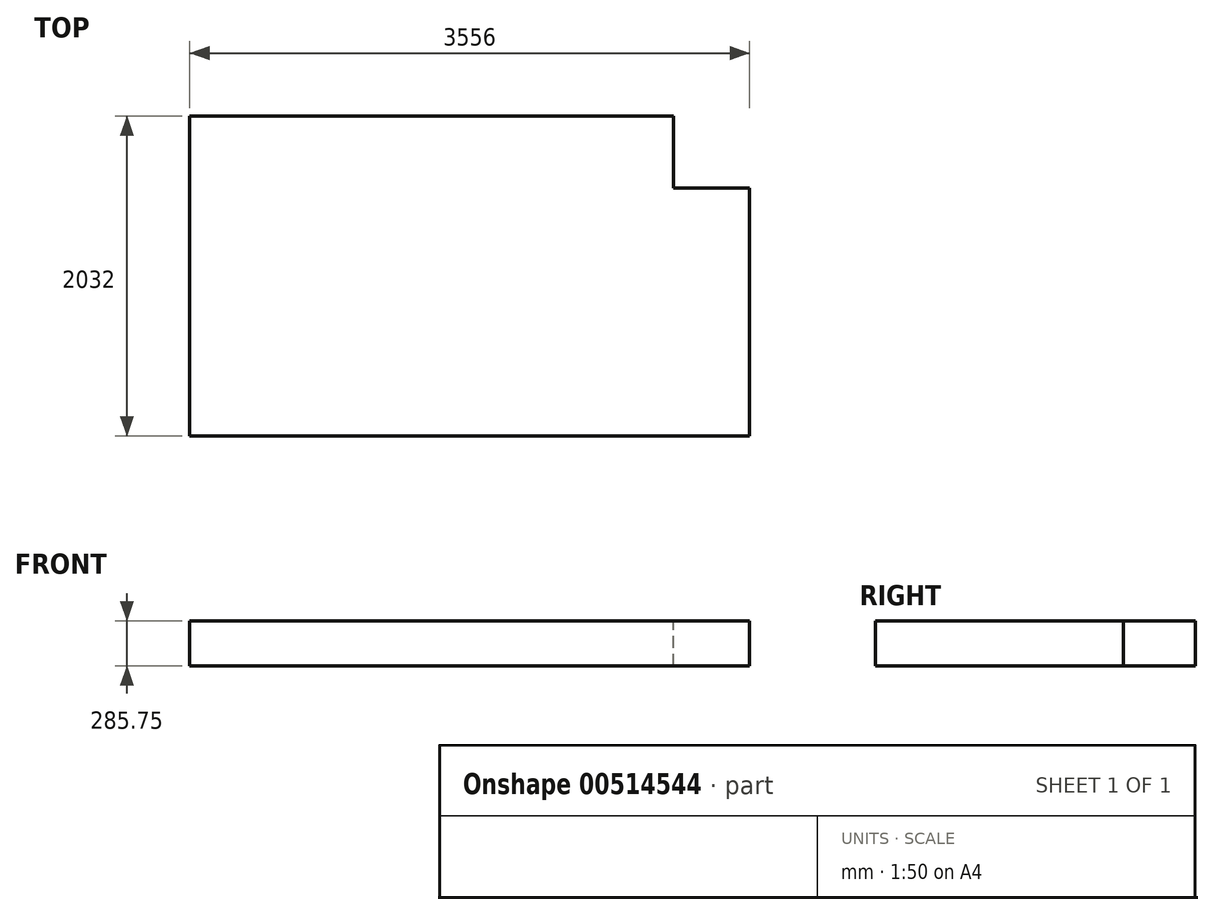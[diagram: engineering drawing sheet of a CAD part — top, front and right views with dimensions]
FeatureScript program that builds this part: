
annotation { "Feature Type Name" : "Feature", "Feature Type Description" : "" }
export const myFeature = defineFeature(function(context is Context, id is Id, definition is map)
    precondition{}
    {
        {
            var Q0;
            Q0=qCreatedBy(makeId("Top.planeOp"),FACE);
            var sketch = newSketch(context, id + "F0", { "sketchPlane" : qUnion([Q0])});
            skLineSegment(sketch, "E0.bottom", {"start": v(1700.43, 1002.82) * mm, "end": v(-1855.57, 1002.82) * mm});
            skLineSegment(sketch, "E0.top", {"start": v(1700.43, -1029.18) * mm, "end": v(-1855.57, -1029.18) * mm});
            skLineSegment(sketch, "E0.left", {"start": v(1700.43, 1002.82) * mm, "end": v(1700.43, -1029.18) * mm});
            skLineSegment(sketch, "E0.right", {"start": v(-1855.57, 1002.82) * mm, "end": v(-1855.57, -1029.18) * mm});
            skPoint(sketch, "E0.middle", {"position": v(-77.57, -13.18) * mm});
            skSolve(sketch);
        }
        {
            var Q0;
            Q0=makeQuery(id+"F0.imprint","IMPRINT",FACE,{"disambiguationData":[TD([[makeQuery(id+"F0.imprint","IMPRINT",EDGE,{"derivedFrom":sQuery(id+"F0.wireOp",EDGE,"E0.bottom")}),1.0]])]});
            extrude(context, id + "F1", {"entities" : qUnion([Q0]), "depth" : 285.75 * mm, "offsetDistance" : 25.4 * mm});
        }
        {
            var Q0;
            Q0=makeQuery(id+"F1.opExtrude","CAP_FACE",FACE,{"disambiguationData":[OSD([sQuery(id+"F0.wireOp",EDGE,"E0.bottom"),sQuery(id+"F0.wireOp",EDGE,"E0.top"),sQuery(id+"F0.wireOp",EDGE,"E0.left"),sQuery(id+"F0.wireOp",EDGE,"E0.right")])],"isStart":false});
            var sketch = newSketch(context, id + "F2", { "sketchPlane" : qUnion([Q0])});
            skLineSegment(sketch, "E1", {"start": v(1700.43, 1002.82) * mm, "end": v(1700.43, 545.62) * mm});
            skLineSegment(sketch, "E2", {"start": v(1700.43, 545.62) * mm, "end": v(1217.83, 545.62) * mm});
            skLineSegment(sketch, "E3", {"start": v(1217.83, 545.62) * mm, "end": v(1217.83, 1002.82) * mm});
            skSolve(sketch);
        }
        {
            var Q0;
            {var subQ0=sQuery(id+"F2.wireOp",EDGE,"E1");Q0=makeQuery(id+"F2.imprint","IMPRINT",FACE,{"disambiguationData":[TD([[makeQuery(id+"F2.imprint","IMPRINT",EDGE,{"derivedFrom":subQ0}),-1.0]])]});}
            extrude(context, id + "F3", {"entities" : qUnion([Q0]), "operationType" : NewBodyOperationType.REMOVE, "oppositeDirection" : true, "depth" : 304.8 * mm, "offsetDistance" : 25.4 * mm});
        }
    });
